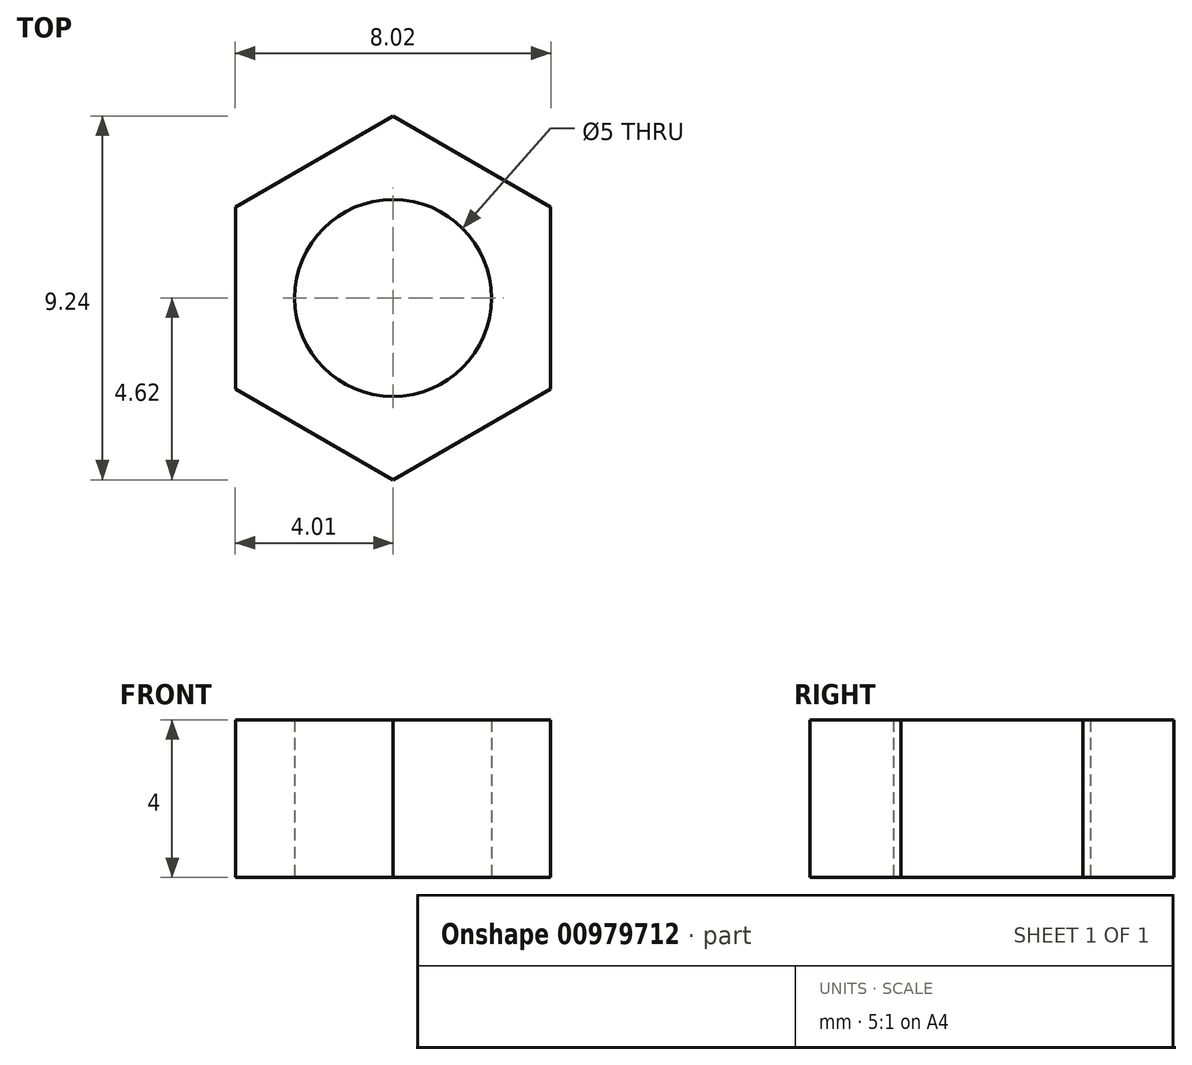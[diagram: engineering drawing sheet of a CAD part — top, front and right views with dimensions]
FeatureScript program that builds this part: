
annotation { "Feature Type Name" : "Feature", "Feature Type Description" : "" }
export const myFeature = defineFeature(function(context is Context, id is Id, definition is map)
    precondition{}
    {
        {
            var Q0;
            Q0=qCreatedBy(makeId("Top.planeOp"),FACE);
            var sketch = newSketch(context, id + "F0", { "sketchPlane" : qUnion([Q0])});
            skCircle(sketch, "E0.cCircle", {"center": v(0, 0) * mm, "radius": 4.63 * mm, "construction": true});
            skLineSegment(sketch, "E0.0", {"start": v(0, 4.62) * mm, "end": v(4, 2.31) * mm});
            skLineSegment(sketch, "E0.1", {"start": v(4, 2.31) * mm, "end": v(4, -2.31) * mm});
            skLineSegment(sketch, "E0.2", {"start": v(4, -2.31) * mm, "end": v(0, -4.62) * mm});
            skLineSegment(sketch, "E0.3", {"start": v(0, -4.63) * mm, "end": v(-4, -2.31) * mm});
            skLineSegment(sketch, "E0.4", {"start": v(-4, -2.31) * mm, "end": v(-4, 2.31) * mm});
            skLineSegment(sketch, "E0.5", {"start": v(-4, 2.31) * mm, "end": v(0, 4.63) * mm});
            skCircle(sketch, "E1", {"center": v(0, 0) * mm, "radius": 2.5 * mm});
            skSolve(sketch);
        }
        {
            var Q0;
            Q0 = qSketchRegion(id + "F0", true);
            extrude(context, id + "F1", {"entities" : qUnion([Q0]), "depth" : 4 * mm, "offsetDistance" : 25 * mm});
        }
    });
